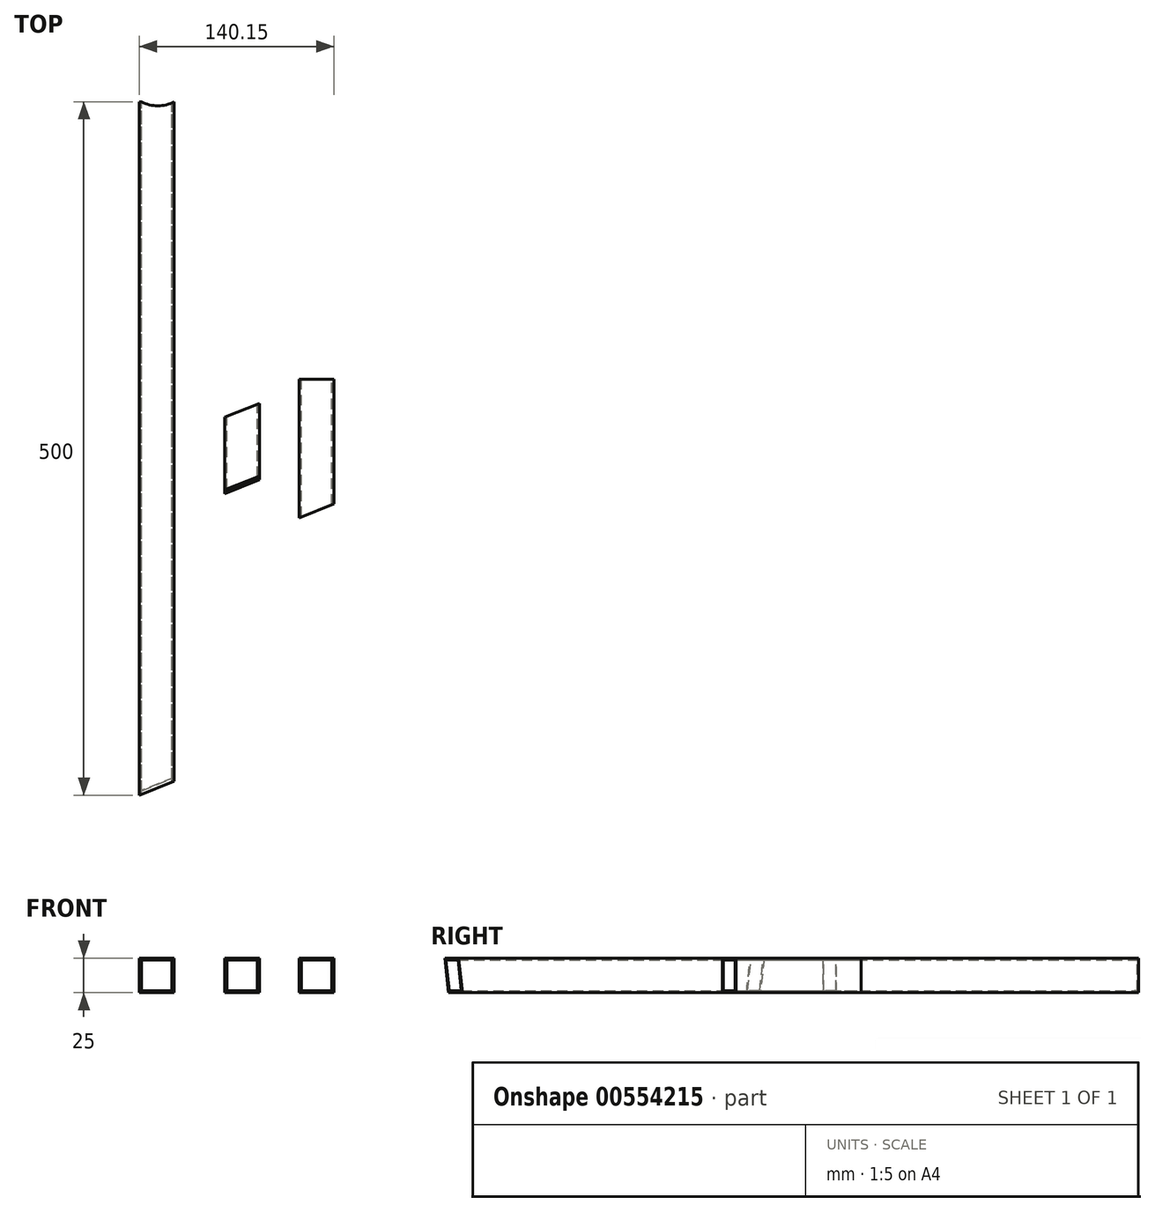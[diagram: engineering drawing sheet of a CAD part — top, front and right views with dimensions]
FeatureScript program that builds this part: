
annotation { "Feature Type Name" : "Feature", "Feature Type Description" : "" }
export const myFeature = defineFeature(function(context is Context, id is Id, definition is map)
    precondition{}
    {
        {
            var Q0;
            Q0=qCreatedBy(makeId("Front.planeOp"),FACE);
            var sketch = newSketch(context, id + "F0", { "sketchPlane" : qUnion([Q0])});
            skLineSegment(sketch, "E0.bottom", {"start": v(-87.5, -12.5) * mm, "end": v(-112.5, -12.5) * mm});
            skLineSegment(sketch, "E0.top", {"start": v(-87.5, 12.5) * mm, "end": v(-112.5, 12.5) * mm});
            skLineSegment(sketch, "E0.left", {"start": v(-87.5, -12.5) * mm, "end": v(-87.5, 12.5) * mm});
            skLineSegment(sketch, "E0.right", {"start": v(-112.5, -12.5) * mm, "end": v(-112.5, 12.5) * mm});
            skPoint(sketch, "E0.middle", {"position": v(-100, 0) * mm});
            skLineSegment(sketch, "E1.0", {"start": v(-111, -11) * mm, "end": v(-111, 11) * mm});
            skLineSegment(sketch, "E1.1", {"start": v(-89, -11) * mm, "end": v(-111, -11) * mm});
            skLineSegment(sketch, "E1.2", {"start": v(-89, -11) * mm, "end": v(-89, 11) * mm});
            skLineSegment(sketch, "E1.3", {"start": v(-89, 11) * mm, "end": v(-111, 11) * mm});
            skSolve(sketch);
        }
        {
            var Q0;
            Q0=makeQuery(id+"F0.imprint","IMPRINT",FACE,{"disambiguationData":[TD([[makeQuery(id+"F0.imprint","IMPRINT",EDGE,{"derivedFrom":sQuery(id+"F0.wireOp",EDGE,"E0.bottom")}),-1.0]])]});
            extrude(context, id + "F1", {"entities" : qUnion([Q0]), "endBound" : BoundingType.SYMMETRIC, "depth" : 500 * mm, "offsetDistance" : 25 * mm});
        }
        {
            var Q0;
            Q0=qCreatedBy(makeId("Front.planeOp"),FACE);
            var sketch = newSketch(context, id + "F2", { "sketchPlane" : qUnion([Q0])});
            skLineSegment(sketch, "E2.bottom", {"start": v(-25.92, -12.5) * mm, "end": v(-50.92, -12.5) * mm});
            skLineSegment(sketch, "E2.top", {"start": v(-25.92, 12.5) * mm, "end": v(-50.92, 12.5) * mm});
            skLineSegment(sketch, "E2.left", {"start": v(-25.92, -12.5) * mm, "end": v(-25.92, 12.5) * mm});
            skLineSegment(sketch, "E2.right", {"start": v(-50.92, -12.5) * mm, "end": v(-50.92, 12.5) * mm});
            skPoint(sketch, "E2.middle", {"position": v(-38.42, 0) * mm});
            skLineSegment(sketch, "E3.0", {"start": v(-49.42, -11) * mm, "end": v(-49.42, 11) * mm});
            skLineSegment(sketch, "E3.1", {"start": v(-27.42, -11) * mm, "end": v(-49.42, -11) * mm});
            skLineSegment(sketch, "E3.2", {"start": v(-27.42, -11) * mm, "end": v(-27.42, 11) * mm});
            skLineSegment(sketch, "E3.3", {"start": v(-27.42, 11) * mm, "end": v(-49.42, 11) * mm});
            skLineSegment(sketch, "E4.bottom", {"start": v(28.78, -12.5) * mm, "end": v(3.78, -12.5) * mm});
            skLineSegment(sketch, "E4.top", {"start": v(28.78, 12.5) * mm, "end": v(3.78, 12.5) * mm});
            skLineSegment(sketch, "E4.left", {"start": v(28.78, -12.5) * mm, "end": v(28.78, 12.5) * mm});
            skLineSegment(sketch, "E4.right", {"start": v(3.78, -12.5) * mm, "end": v(3.78, 12.5) * mm});
            skPoint(sketch, "E4.middle", {"position": v(16.28, 0) * mm});
            skLineSegment(sketch, "E5.0", {"start": v(5.28, -11) * mm, "end": v(5.28, 11) * mm});
            skLineSegment(sketch, "E5.1", {"start": v(27.28, -11) * mm, "end": v(5.28, -11) * mm});
            skLineSegment(sketch, "E5.2", {"start": v(27.28, -11) * mm, "end": v(27.28, 11) * mm});
            skLineSegment(sketch, "E5.3", {"start": v(27.28, 11) * mm, "end": v(5.28, 11) * mm});
            skSolve(sketch);
        }
        {
            var Q0;
            Q0=makeQuery(id+"F2.imprint","IMPRINT",FACE,{"disambiguationData":[TD([[makeQuery(id+"F2.imprint","IMPRINT",EDGE,{"derivedFrom":sQuery(id+"F2.wireOp",EDGE,"E2.bottom")}),-1.0]])]});
            extrude(context, id + "F3", {"entities" : qUnion([Q0]), "endBound" : BoundingType.SYMMETRIC, "depth" : 65 * mm, "offsetDistance" : 25 * mm});
        }
        {
            var Q0;
            Q0=qCreatedBy(makeId("Front.planeOp"),FACE);
            var sketch = newSketch(context, id + "F4", { "sketchPlane" : qUnion([Q0])});
            skLineSegment(sketch, "E6.bottom", {"start": v(27.65, -12.5) * mm, "end": v(2.65, -12.5) * mm});
            skLineSegment(sketch, "E6.top", {"start": v(27.65, 12.5) * mm, "end": v(2.65, 12.5) * mm});
            skLineSegment(sketch, "E6.left", {"start": v(27.65, -12.5) * mm, "end": v(27.65, 12.5) * mm});
            skLineSegment(sketch, "E6.right", {"start": v(2.65, -12.5) * mm, "end": v(2.65, 12.5) * mm});
            skPoint(sketch, "E6.middle", {"position": v(15.15, 0) * mm});
            skLineSegment(sketch, "E7.0", {"start": v(4.15, -11) * mm, "end": v(4.15, 11) * mm});
            skLineSegment(sketch, "E7.1", {"start": v(26.15, -11) * mm, "end": v(4.15, -11) * mm});
            skLineSegment(sketch, "E7.2", {"start": v(26.15, -11) * mm, "end": v(26.15, 11) * mm});
            skLineSegment(sketch, "E7.3", {"start": v(26.15, 11) * mm, "end": v(4.15, 11) * mm});
            skSolve(sketch);
        }
        {
            var Q0;
            Q0=makeQuery(id+"F4.imprint","IMPRINT",FACE,{"disambiguationData":[TD([[makeQuery(id+"F4.imprint","IMPRINT",EDGE,{"derivedFrom":sQuery(id+"F4.wireOp",EDGE,"E6.bottom")}),-1.0]])]});
            extrude(context, id + "F5", {"entities" : qUnion([Q0]), "endBound" : BoundingType.SYMMETRIC, "depth" : 100 * mm, "offsetDistance" : 25 * mm});
        }
        {
            var Q0;
            Q0=makeQuery(id+"F1.opExtrude","CAP_EDGE",EDGE,{"disambiguationData":[OSD([sQuery(id+"F0.wireOp",EDGE,"E0.left")])],"isStart":false});
            var Q1;
            Q1=makeQuery(id+"F3.opExtrude","CAP_EDGE",EDGE,{"disambiguationData":[OSD([sQuery(id+"F2.wireOp",EDGE,"E2.left")])],"isStart":false});
            var Q2;
            Q2=makeQuery(id+"F3.opExtrude","CAP_EDGE",EDGE,{"disambiguationData":[OSD([sQuery(id+"F2.wireOp",EDGE,"E2.right")])],"isStart":true});
            var Q3;
            Q3=makeQuery(id+"F5.opExtrude","CAP_EDGE",EDGE,{"disambiguationData":[OSD([sQuery(id+"F4.wireOp",EDGE,"E6.left")])],"isStart":false});
            chamfer(context, id + "F6", {"entities" : qUnion([Q0, Q1, Q2, Q3]), "chamferType" : ChamferType.TWO_OFFSETS, "width1" : 25 * mm, "oppositeDirection" : false, "width2" : 10 * mm, "tangentPropagation" : true});
        }
        {
            var Q0;
            Q0=makeQuery(id+"F1.opExtrude","SWEPT_FACE",FACE,{"disambiguationData":[OSD([sQuery(id+"F0.wireOp",EDGE,"E0.top")])]});
            var sketch = newSketch(context, id + "F7", { "sketchPlane" : qUnion([Q0])});
            skCircle(sketch, "E8", {"center": v(-99.25, 272.07) * mm, "radius": 25 * mm});
            skSolve(sketch);
        }
        {
            var Q0;
            Q0 = qSketchRegion(id + "F7", true);
            extrude(context, id + "F8", {"entities" : qUnion([Q0]), "operationType" : NewBodyOperationType.REMOVE, "oppositeDirection" : true, "depth" : 25 * mm, "offsetDistance" : 25 * mm});
        }
        {
            var Q0;
            Q0=makeQuery(id+"F6.opChamfer","BLEND_EDGE",EDGE,{"blendedFrom":[makeQuery(id+"F1.opExtrude","CAP_EDGE",EDGE,{"disambiguationData":[OSD([sQuery(id+"F0.wireOp",EDGE,"E0.left")])],"isStart":false}),makeQuery(id+"F1.opExtrude","SWEPT_FACE",FACE,{"disambiguationData":[OSD([sQuery(id+"F0.wireOp",EDGE,"E0.bottom")])]})],"blendedInto":[makeQuery(id+"F1.opExtrude","SWEPT_FACE",FACE,{"disambiguationData":[OSD([sQuery(id+"F0.wireOp",EDGE,"E0.bottom")])]})]});
            chamfer(context, id + "F9", {"entities" : qUnion([Q0]), "chamferType" : ChamferType.TWO_OFFSETS, "width1" : 2.5 * mm, "oppositeDirection" : false, "width2" : 25 * mm, "tangentPropagation" : true});
        }
        {
            var Q0;
            Q0=makeQuery(id+"F6.opChamfer","BLEND_EDGE",EDGE,{"blendedFrom":[makeQuery(id+"F3.opExtrude","CAP_EDGE",EDGE,{"disambiguationData":[OSD([sQuery(id+"F2.wireOp",EDGE,"E2.left")])],"isStart":false}),makeQuery(id+"F3.opExtrude","SWEPT_FACE",FACE,{"disambiguationData":[OSD([sQuery(id+"F2.wireOp",EDGE,"E2.top")])]})],"blendedInto":[makeQuery(id+"F3.opExtrude","SWEPT_FACE",FACE,{"disambiguationData":[OSD([sQuery(id+"F2.wireOp",EDGE,"E2.top")])]})]});
            chamfer(context, id + "F10", {"entities" : qUnion([Q0]), "chamferType" : ChamferType.TWO_OFFSETS, "width1" : 2.5 * mm, "oppositeDirection" : false, "width2" : 25 * mm, "tangentPropagation" : true});
        }
    });
